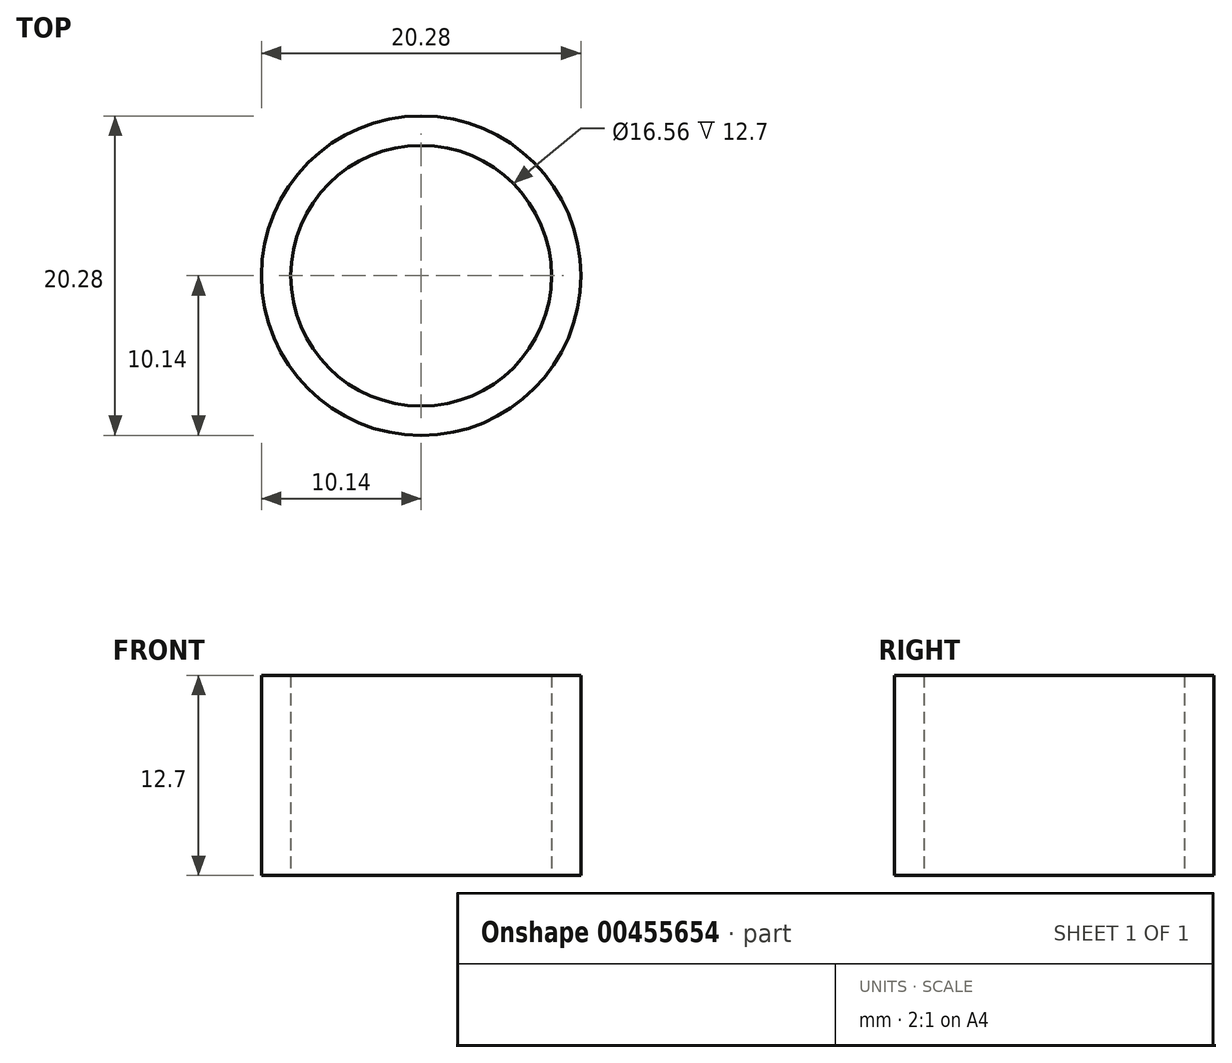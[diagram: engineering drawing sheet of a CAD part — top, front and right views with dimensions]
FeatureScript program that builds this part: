
annotation { "Feature Type Name" : "Feature", "Feature Type Description" : "" }
export const myFeature = defineFeature(function(context is Context, id is Id, definition is map)
    precondition{}
    {
        {
            var Q0;
            Q0=qCreatedBy(makeId("Top.planeOp"),FACE);
            var sketch = newSketch(context, id + "F0", { "sketchPlane" : qUnion([Q0])});
            skCircle(sketch, "E0", {"center": v(0, 0) * mm, "radius": 8.28 * mm});
            skCircle(sketch, "E1", {"center": v(0, 0) * mm, "radius": 10.14 * mm});
            skSolve(sketch);
        }
        {
            var Q0;
            Q0=makeQuery(id+"F0.imprint","IMPRINT",FACE,{"disambiguationData":[TD([[makeQuery(id+"F0.imprint","IMPRINT",EDGE,{"derivedFrom":sQuery(id+"F0.wireOp",EDGE,"E0")}),-1.0]])]});
            extrude(context, id + "F1", {"entities" : qUnion([Q0]), "depth" : 12.7 * mm});
        }
    });
